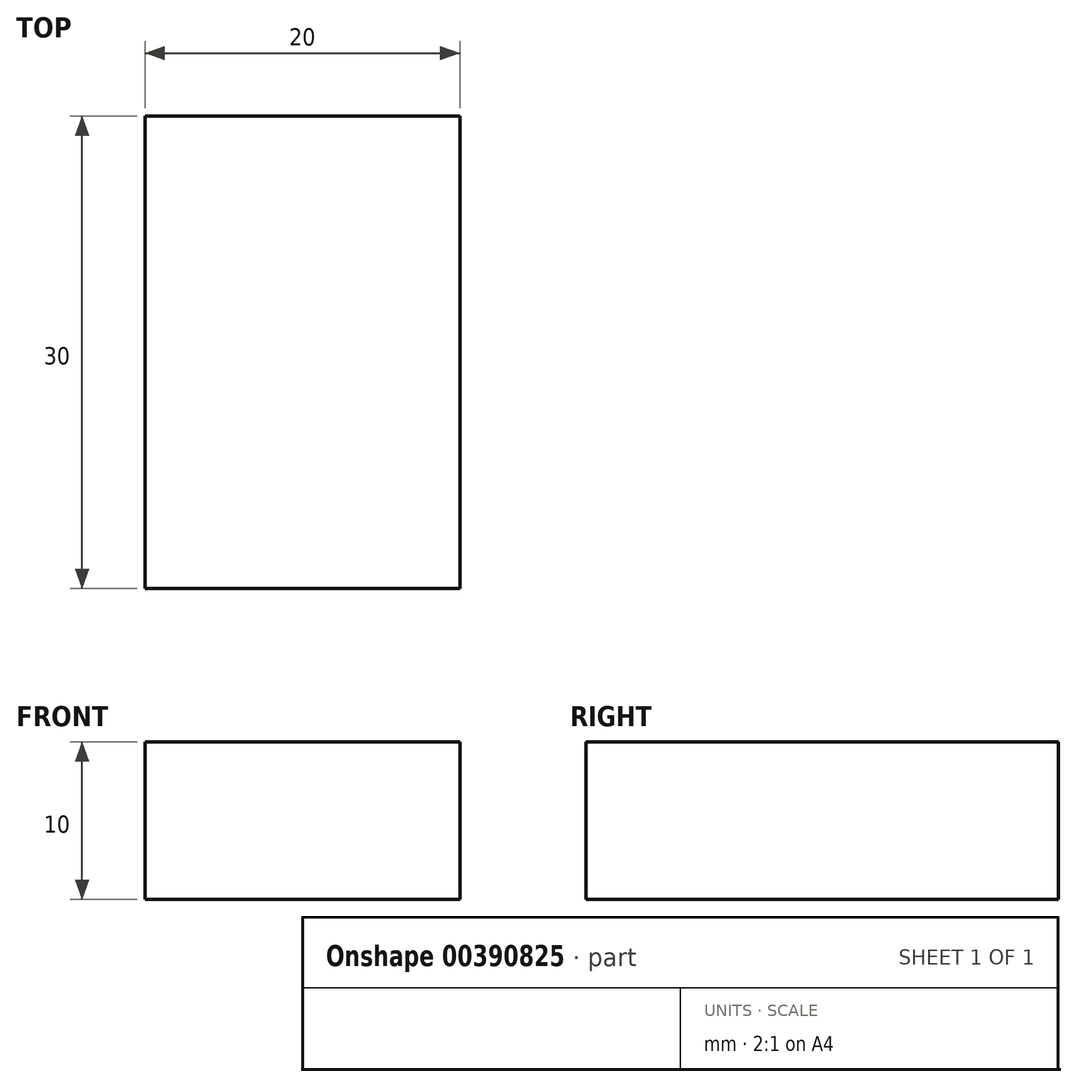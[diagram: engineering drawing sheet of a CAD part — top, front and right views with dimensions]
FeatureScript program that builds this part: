
annotation { "Feature Type Name" : "Feature", "Feature Type Description" : "" }
export const myFeature = defineFeature(function(context is Context, id is Id, definition is map)
    precondition{}
    {
        {
            var Q0;
            Q0=qCreatedBy(makeId("Top.planeOp"),FACE);
            var sketch = newSketch(context, id + "F0", { "sketchPlane" : qUnion([Q0])});
            skLineSegment(sketch, "E0.bottom", {"start": v(0, 0) * mm, "end": v(20, 0) * mm});
            skLineSegment(sketch, "E0.top", {"start": v(0, 30) * mm, "end": v(20, 30) * mm});
            skLineSegment(sketch, "E0.left", {"start": v(0, 0) * mm, "end": v(0, 30) * mm});
            skLineSegment(sketch, "E0.right", {"start": v(20, 0) * mm, "end": v(20, 30) * mm});
            skSolve(sketch);
        }
        {
            var Q0;
            Q0 = qSketchRegion(id + "F0", true);
            extrude(context, id + "F1", {"entities" : qUnion([Q0]), "flatOperationType" : FlatOperationType.REMOVE, "offsetDistance" : 25 * mm, "depth" : 10 * mm, "domain" : OperationDomain.MODEL});
        }
    });
